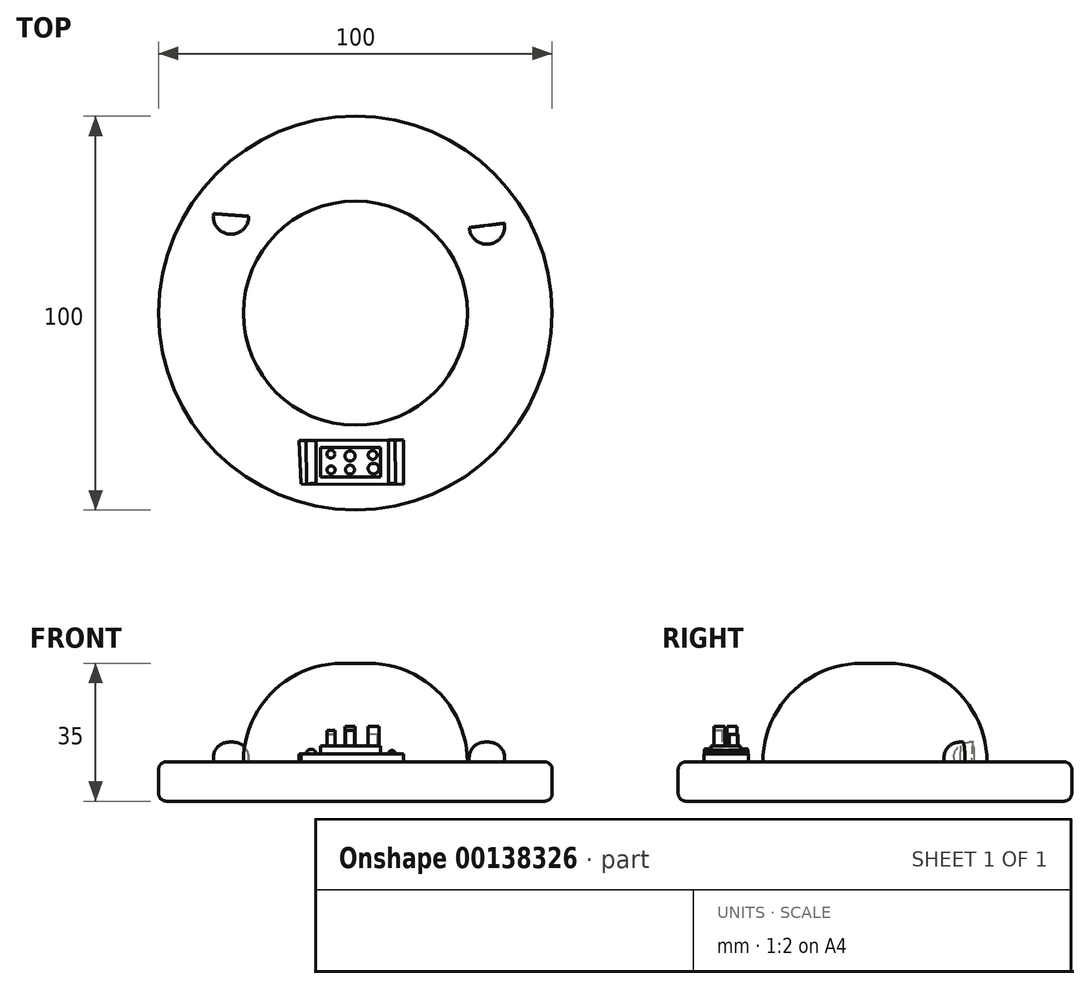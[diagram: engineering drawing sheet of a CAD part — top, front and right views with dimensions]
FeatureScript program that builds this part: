
annotation { "Feature Type Name" : "Feature", "Feature Type Description" : "" }
export const myFeature = defineFeature(function(context is Context, id is Id, definition is map)
    precondition{}
    {
        {
            var Q0;
            Q0=qCreatedBy(makeId("Top.planeOp"),FACE);
            var sketch = newSketch(context, id + "F0", { "sketchPlane" : qUnion([Q0])});
            skCircle(sketch, "E0", {"center": v(0, 0) * mm, "radius": 50 * mm});
            skSolve(sketch);
        }
        {
            var Q0;
            Q0 = qSketchRegion(id + "F0", true);
            extrude(context, id + "F1", {"entities" : qUnion([Q0]), "depth" : 10 * mm});
        }
        {
            var Q0;
            Q0=makeQuery(id+"F1.opExtrude","CAP_EDGE",EDGE,{"disambiguationData":[OSD([sQuery(id+"F0.wireOp",EDGE,"E0")])],"isStart":false});
            var Q1;
            Q1=makeQuery(id+"F1.opExtrude","CAP_EDGE",EDGE,{"disambiguationData":[OSD([sQuery(id+"F0.wireOp",EDGE,"E0")])],"isStart":true});
            fillet(context, id + "F2", {"entities" : qUnion([Q0, Q1]), "radius" : 2 * mm, "tangentPropagation" : true, "allowEdgeOverflow" : false});
        }
        {
            var Q0;
            Q0=makeQuery(id+"F1.opExtrude","CAP_FACE",FACE,{"disambiguationData":[OSD([sQuery(id+"F0.wireOp",EDGE,"E0")])],"isStart":false});
            var sketch = newSketch(context, id + "F3", { "sketchPlane" : qUnion([Q0])});
            skCircle(sketch, "E1", {"center": v(0, 0) * mm, "radius": 28.46 * mm});
            skSolve(sketch);
        }
        {
            var Q0;
            Q0 = qSketchRegion(id + "F3", true);
            extrude(context, id + "F4", {"entities" : qUnion([Q0]), "operationType" : NewBodyOperationType.ADD, "depth" : 25 * mm});
        }
        {
            var Q0;
            Q0=makeQuery(id+"F4.opExtrude","CAP_EDGE",EDGE,{"disambiguationData":[OSD([sQuery(id+"F3.wireOp",EDGE,"E1")])],"isStart":false});
            fillet(context, id + "F5", {"entities" : qUnion([Q0]), "radius" : 25 * mm, "tangentPropagation" : true, "allowEdgeOverflow" : false});
        }
        {
            var Q0;
            Q0=makeQuery(id+"F1.opExtrude","CAP_FACE",FACE,{"disambiguationData":[OSD([sQuery(id+"F0.wireOp",EDGE,"E0")])],"isStart":false});
            var sketch = newSketch(context, id + "F6", { "sketchPlane" : qUnion([Q0])});
            skCircle(sketch, "E2", {"center": v(-31.6, 24.53) * mm, "radius": 4.5 * mm});
            skCircle(sketch, "E3", {"center": v(33.4, 22) * mm, "radius": 4.5 * mm});
            skSolve(sketch);
        }
        {
            var Q0;
            Q0=makeQuery(id+"F6.imprint","IMPRINT",FACE,{"disambiguationData":[TD([[makeQuery(id+"F6.imprint","IMPRINT",EDGE,{"derivedFrom":sQuery(id+"F6.wireOp",EDGE,"E2")}),1.0]])]});
            var Q1;
            Q1=makeQuery(id+"F6.imprint","IMPRINT",FACE,{"disambiguationData":[TD([[makeQuery(id+"F6.imprint","IMPRINT",EDGE,{"derivedFrom":sQuery(id+"F6.wireOp",EDGE,"E2")}),1.0]])]});
            var Q2;
            Q2=makeQuery(id+"F6.imprint","IMPRINT",FACE,{"disambiguationData":[TD([[makeQuery(id+"F6.imprint","IMPRINT",EDGE,{"derivedFrom":sQuery(id+"F6.wireOp",EDGE,"E3")}),1.0]])]});
            extrude(context, id + "F7", {"entities" : qUnion([Q0, Q1, Q2]), "operationType" : NewBodyOperationType.ADD, "depth" : 5 * mm});
        }
        {
            var Q0;
            Q0=makeQuery(id+"F7.opExtrude","CAP_FACE",FACE,{"disambiguationData":[OSD([sQuery(id+"F6.wireOp",EDGE,"E3")])],"isStart":false});
            var sketch = newSketch(context, id + "F8", { "sketchPlane" : qUnion([Q0])});
            skArc(sketch, "E4", {"start": v(37.83, 22.84) * mm, "mid": v(32.84, 26.61) * mm, "end": v(28.91, 21.74) * mm});
            skLineSegment(sketch, "E5", {"start": v(28.91, 21.74) * mm, "end": v(37.83, 22.84) * mm});
            skSolve(sketch);
        }
        {
            var Q0;
            Q0 = qSketchRegion(id + "F8", true);
            var Q1;
            {var subQ0=sQuery(id+"F8.wireOp",EDGE,"E5");Q1=makeQuery(id+"F8.imprint","IMPRINT",FACE,{"disambiguationData":[TD([[makeQuery(id+"F8.imprint","IMPRINT",EDGE,{"derivedFrom":subQ0}),1.0]])]});}
            extrude(context, id + "F9", {"entities" : qUnion([Q0, Q1]), "operationType" : NewBodyOperationType.REMOVE, "oppositeDirection" : true, "depth" : 5 * mm});
        }
        {
            var Q0;
            Q0=makeQuery(id+"F7.opExtrude","CAP_EDGE",EDGE,{"disambiguationData":[OSD([sQuery(id+"F6.wireOp",EDGE,"E3")])],"isStart":false});
            fillet(context, id + "F10", {"entities" : qUnion([Q0]), "radius" : 4 * mm, "tangentPropagation" : true, "allowEdgeOverflow" : false});
        }
        {
            var Q0;
            Q0=makeQuery(id+"F7.opExtrude","CAP_FACE",FACE,{"disambiguationData":[OSD([sQuery(id+"F6.wireOp",EDGE,"E2")])],"isStart":false});
            var sketch = newSketch(context, id + "F11", { "sketchPlane" : qUnion([Q0])});
            skArc(sketch, "E6", {"start": v(-27.1, 24.6) * mm, "mid": v(-31.26, 29.11) * mm, "end": v(-36.04, 25.26) * mm});
            skLineSegment(sketch, "E7", {"start": v(-36.04, 25.26) * mm, "end": v(-27.1, 24.6) * mm});
            skSolve(sketch);
        }
        {
            var Q0;
            Q0 = qSketchRegion(id + "F11", true);
            var Q1;
            {var subQ0=sQuery(id+"F11.wireOp",EDGE,"E7");Q1=makeQuery(id+"F11.imprint","IMPRINT",FACE,{"disambiguationData":[TD([[makeQuery(id+"F11.imprint","IMPRINT",EDGE,{"derivedFrom":subQ0}),1.0]])]});}
            extrude(context, id + "F12", {"entities" : qUnion([Q0, Q1]), "operationType" : NewBodyOperationType.REMOVE, "oppositeDirection" : true, "depth" : 5 * mm});
        }
        {
            var Q0;
            Q0=makeQuery(id+"F7.opExtrude","CAP_EDGE",EDGE,{"disambiguationData":[OSD([sQuery(id+"F6.wireOp",EDGE,"E2")])],"isStart":false});
            fillet(context, id + "F13", {"entities" : qUnion([Q0]), "radius" : 4 * mm, "tangentPropagation" : true, "allowEdgeOverflow" : false});
        }
        {
            var Q0;
            Q0=makeQuery(id+"F12.boolean.opBoolean","MERGE",FACE,{"derivedFrom":[makeQuery(id+"F9.boolean.opBoolean","MERGE",FACE,{"derivedFrom":[makeQuery(id+"F1.opExtrude","CAP_FACE",FACE,{"disambiguationData":[OSD([sQuery(id+"F0.wireOp",EDGE,"E0")])],"isStart":false}),makeQuery(id+"F9.opExtrude","CAP_FACE",FACE,{"disambiguationData":[OSD([sQuery(id+"F8.wireOp",EDGE,"E4"),sQuery(id+"F8.wireOp",EDGE,"E5")])],"isStart":false})]}),makeQuery(id+"F12.opExtrude","CAP_FACE",FACE,{"disambiguationData":[OSD([sQuery(id+"F11.wireOp",EDGE,"E6"),sQuery(id+"F11.wireOp",EDGE,"E7")])],"isStart":false})]});
            var sketch = newSketch(context, id + "F14", { "sketchPlane" : qUnion([Q0])});
            skLineSegment(sketch, "E8", {"start": v(12.29, -43.49) * mm, "end": v(12.29, -32.2) * mm});
            skLineSegment(sketch, "E9", {"start": v(12.29, -32.2) * mm, "end": v(-14.28, -32.36) * mm});
            skLineSegment(sketch, "E10", {"start": v(-14.28, -32.36) * mm, "end": v(-13.75, -43.44) * mm});
            skLineSegment(sketch, "E11", {"start": v(-13.75, -43.44) * mm, "end": v(12.29, -43.49) * mm});
            skSolve(sketch);
        }
        {
            var Q0;
            Q0 = qSketchRegion(id + "F14", true);
            var Q1;
            Q1=makeQuery(id+"F14.imprint","IMPRINT",FACE,{"disambiguationData":[TD([[makeQuery(id+"F14.imprint","IMPRINT",EDGE,{"derivedFrom":sQuery(id+"F14.wireOp",EDGE,"E8")}),1.0]])]});
            extrude(context, id + "F15", {"entities" : qUnion([Q0, Q1]), "operationType" : NewBodyOperationType.ADD, "depth" : 2 * mm});
        }
        {
            var Q0;
            Q0=makeQuery(id+"F15.opExtrude","SWEPT_FACE",FACE,{"disambiguationData":[OSD([sQuery(id+"F14.wireOp",EDGE,"E9")])]});
            var sketch = newSketch(context, id + "F16", { "sketchPlane" : qUnion([Q0])});
            skCircle(sketch, "E12", {"center": v(-9.08, 12) * mm, "radius": 0.86 * mm});
            skCircle(sketch, "E13", {"center": v(11.47, 12) * mm, "radius": 1.22 * mm});
            skSolve(sketch);
        }
        {
            var Q0;
            Q0 = qSketchRegion(id + "F16", true);
            extrude(context, id + "F17", {"entities" : qUnion([Q0]), "operationType" : NewBodyOperationType.ADD, "oppositeDirection" : true, "depth" : 11 * mm});
        }
        {
            var Q0;
            Q0=makeQuery(id+"F15.opExtrude","CAP_FACE",FACE,{"disambiguationData":[OSD([sQuery(id+"F14.wireOp",EDGE,"E8"),sQuery(id+"F14.wireOp",EDGE,"E9"),sQuery(id+"F14.wireOp",EDGE,"E10"),sQuery(id+"F14.wireOp",EDGE,"E11")])],"isStart":false});
            var sketch = newSketch(context, id + "F18", { "sketchPlane" : qUnion([Q0])});
            skLineSegment(sketch, "E14.bottom", {"start": v(6.43, -41.65) * mm, "end": v(-8.88, -41.65) * mm});
            skLineSegment(sketch, "E14.top", {"start": v(6.43, -34.16) * mm, "end": v(-8.88, -34.16) * mm});
            skLineSegment(sketch, "E14.left", {"start": v(6.43, -41.65) * mm, "end": v(6.43, -34.16) * mm});
            skLineSegment(sketch, "E14.right", {"start": v(-8.88, -41.65) * mm, "end": v(-8.88, -34.16) * mm});
            skSolve(sketch);
        }
        {
            var Q0;
            Q0 = qSketchRegion(id + "F18", true);
            extrude(context, id + "F19", {"entities" : qUnion([Q0]), "operationType" : NewBodyOperationType.ADD, "depth" : 2 * mm});
        }
        {
            var Q0;
            Q0=makeQuery(id+"F19.opExtrude","CAP_FACE",FACE,{"disambiguationData":[OSD([sQuery(id+"F18.wireOp",EDGE,"E14.bottom"),sQuery(id+"F18.wireOp",EDGE,"E14.top"),sQuery(id+"F18.wireOp",EDGE,"E14.left"),sQuery(id+"F18.wireOp",EDGE,"E14.right")])],"isStart":false});
            var sketch = newSketch(context, id + "F20", { "sketchPlane" : qUnion([Q0])});
            skCircle(sketch, "E15", {"center": v(4.61, -39.5) * mm, "radius": 1.36 * mm});
            skCircle(sketch, "E16", {"center": v(4.38, -36.04) * mm, "radius": 1.12 * mm});
            skCircle(sketch, "E17", {"center": v(-1.37, -39.78) * mm, "radius": 1.14 * mm});
            skCircle(sketch, "E18", {"center": v(-1.37, -36.3) * mm, "radius": 1.28 * mm});
            skCircle(sketch, "E19", {"center": v(-6.2, -39.83) * mm, "radius": 1 * mm});
            skCircle(sketch, "E20", {"center": v(-6.24, -35.8) * mm, "radius": 1 * mm});
            skSolve(sketch);
        }
        {
            var Q0;
            Q0=makeQuery(id+"F20.imprint","IMPRINT",FACE,{"disambiguationData":[TD([[makeQuery(id+"F20.imprint","IMPRINT",EDGE,{"derivedFrom":sQuery(id+"F20.wireOp",EDGE,"E15")}),1.0]])]});
            var Q1;
            Q1=makeQuery(id+"F20.imprint","IMPRINT",FACE,{"disambiguationData":[TD([[makeQuery(id+"F20.imprint","IMPRINT",EDGE,{"derivedFrom":sQuery(id+"F20.wireOp",EDGE,"E18")}),1.0]])]});
            extrude(context, id + "F21", {"entities" : qUnion([Q0, Q1]), "operationType" : NewBodyOperationType.ADD, "depth" : 5 * mm});
        }
        {
            var Q0;
            Q0=makeQuery(id+"F20.imprint","IMPRINT",FACE,{"disambiguationData":[TD([[makeQuery(id+"F20.imprint","IMPRINT",EDGE,{"derivedFrom":sQuery(id+"F20.wireOp",EDGE,"E20")}),1.0]])]});
            var Q1;
            Q1=makeQuery(id+"F20.imprint","IMPRINT",FACE,{"disambiguationData":[TD([[makeQuery(id+"F20.imprint","IMPRINT",EDGE,{"derivedFrom":sQuery(id+"F20.wireOp",EDGE,"E16")}),1.0]])]});
            extrude(context, id + "F22", {"entities" : qUnion([Q0, Q1]), "operationType" : NewBodyOperationType.ADD, "depth" : 3 * mm});
        }
        {
            var Q0;
            Q0=makeQuery(id+"F20.imprint","IMPRINT",FACE,{"disambiguationData":[TD([[makeQuery(id+"F20.imprint","IMPRINT",EDGE,{"derivedFrom":sQuery(id+"F20.wireOp",EDGE,"E19")}),1.0]])]});
            var Q1;
            Q1=makeQuery(id+"F20.imprint","IMPRINT",FACE,{"disambiguationData":[TD([[makeQuery(id+"F20.imprint","IMPRINT",EDGE,{"derivedFrom":sQuery(id+"F20.wireOp",EDGE,"E17")}),1.0]])]});
            extrude(context, id + "F23", {"entities" : qUnion([Q0, Q1]), "operationType" : NewBodyOperationType.ADD, "depth" : 4 * mm});
        }
    });
